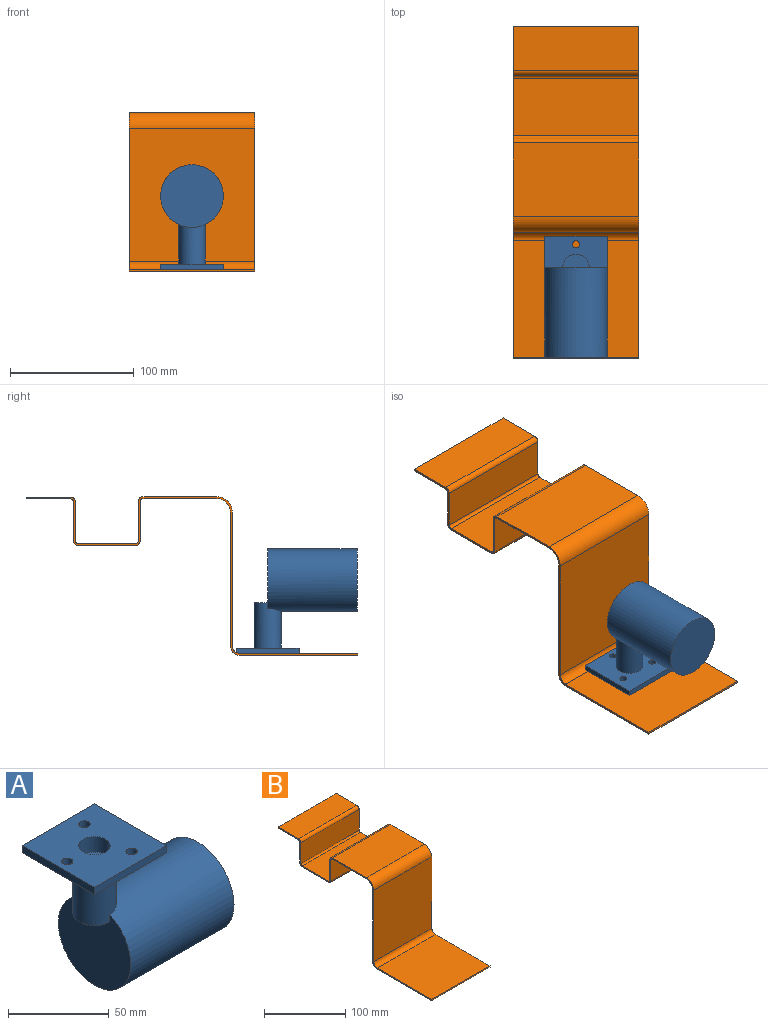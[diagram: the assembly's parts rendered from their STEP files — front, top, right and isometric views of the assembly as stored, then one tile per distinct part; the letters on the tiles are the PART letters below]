
ASSEMBLY  parts=2 mates=1
PART A: 16 faces, bbox 97.8x50.8x84.8 mm
  f0: cylinder r=10.82mm len=36.53mm, axis (0,0,1), area 2291.1mm2, adj f1,f6,f8,f10
  f1: plane 21.65x10.82mm, normal (0,0,-1), area 184mm2, adj f0,f10
  f2: plane 50.8x4.37mm, normal (0,1,0), area 221.9mm2, adj f3,f5,f6,f7
  f3: plane 50.8x4.37mm, normal (-1,0,0), area 221.9mm2, adj f2,f4,f6,f7
  f4: plane 50.8x4.37mm, normal (0,-1,0), area 221.9mm2, adj f3,f5,f6,f7
  f5: plane 50.8x4.37mm, normal (1,0,0), area 221.9mm2, adj f2,f4,f6,f7
  f6: plane 50.8x50.8mm, normal (0,0,-1), area 2138.6mm2, adj f0,f2,f3,f4,f5,f13,f14,f15
  f7: plane 50.8x50.8mm, normal (0,0,1), area 2316mm2, adj f2,f3,f4,f5,f11,f13,f14,f15
  f8: cylinder r=25.37mm len=72.39mm, axis (-1,0,0), area 11349.6mm2, adj f0,f9,f10
  f9: plane 50.74x50.74mm, normal (1,0,0), area 2021.6mm2, adj f8
  f10: plane 50.74x48.31mm, normal (-1,0,0), area 1890.1mm2, adj f0,f1,f8
  f11: cylinder r=7.79mm len=15.58mm, axis (0,0,1), area 459.9mm2, adj f7,f12
  f12: plane 15.58x15.58mm, normal (0,0,1), area 190.6mm2, adj f11
  f13: cylinder r=2.8mm len=5.61mm, axis (0,0,1), area 76.9mm2, adj f6,f7
  f14: cylinder r=2.8mm len=5.61mm, axis (0,0,1), area 76.9mm2, adj f6,f7
  f15: cylinder r=2.8mm len=5.61mm, axis (0,0,1), area 76.9mm2, adj f6,f7
PART B: 54 faces, bbox 101.6x268.5x128.6 mm
  f0: plane 95.25x1.59mm, normal (-1,0,0), area 151.2mm2, adj f2,f3,f4,f50
  f1: plane 95.25x1.59mm, normal (1,0,0), area 151.2mm2, adj f2,f3,f4,f51
  f2: plane 101.6x1.59mm, normal (0,-1,0), area 161.3mm2, adj f0,f1,f3,f4
  f3: plane 101.6x95.25mm, normal (0,0,-1), area 9677.4mm2, adj f0,f1,f2,f52
  f4: plane 101.6x95.25mm, normal (0,0,1), area 9677.4mm2, adj f0,f1,f2,f53
  f5: plane 107.95x1.59mm, normal (-1,0,0), area 171.4mm2, adj f7,f8,f46,f50
  f6: plane 107.95x1.59mm, normal (1,0,0), area 171.4mm2, adj f7,f8,f47,f51
  f7: plane 107.95x101.6mm, normal (0,1,0), area 10967.7mm2, adj f5,f6,f48,f52
  f8: plane 107.95x101.6mm, normal (0,-1,0), area 10967.7mm2, adj f5,f6,f49,f53
  f9: plane 59.63x1.59mm, normal (-1,0,0), area 94.7mm2, adj f11,f12,f43,f46
  f10: plane 59.63x1.59mm, normal (1,0,0), area 94.7mm2, adj f11,f12,f42,f47
  f11: plane 101.6x59.63mm, normal (0,0,-1), area 6058.1mm2, adj f9,f10,f45,f48
  f12: plane 101.6x59.63mm, normal (0,0,1), area 6058.1mm2, adj f9,f10,f44,f49
  f13: plane 31.94x1.59mm, normal (-1,0,0), area 50.7mm2, adj f15,f16,f39,f43
  f14: plane 31.94x1.59mm, normal (1,0,0), area 50.7mm2, adj f15,f16,f38,f42
  f15: plane 101.6x31.94mm, normal (0,-1,0), area 3245.2mm2, adj f13,f14,f40,f45
  f16: plane 101.6x31.94mm, normal (0,1,0), area 3245.2mm2, adj f13,f14,f41,f44
  f17: plane 46.23x1.59mm, normal (-1,0,0), area 73.4mm2, adj f19,f20,f35,f39
  f18: plane 46.23x1.59mm, normal (1,0,0), area 73.4mm2, adj f19,f20,f34,f38
  f19: plane 101.6x46.23mm, normal (0,0,-1), area 4696.8mm2, adj f17,f18,f36,f40
  f20: plane 101.6x46.23mm, normal (0,0,1), area 4696.8mm2, adj f17,f18,f37,f41
  f21: plane 31.58x1.59mm, normal (-1,0,0), area 50.1mm2, adj f23,f24,f31,f35
  f22: plane 31.58x1.59mm, normal (1,0,0), area 50.1mm2, adj f23,f24,f30,f34
  f23: plane 101.6x31.58mm, normal (0,1,0), area 3208.3mm2, adj f21,f22,f33,f36
  f24: plane 101.6x31.58mm, normal (0,-1,0), area 3208.3mm2, adj f21,f22,f32,f37
  f25: plane 36.04x1.59mm, normal (-1,0,0), area 57.2mm2, adj f26,f28,f29,f31
  f26: plane 101.6x1.59mm, normal (0,1,0), area 161.3mm2, adj f25,f27,f28,f29
  f27: plane 36.04x1.59mm, normal (1,0,0), area 57.2mm2, adj f26,f28,f29,f30
  f28: plane 101.6x36.04mm, normal (0,0,-1), area 3661.7mm2, adj f25,f26,f27,f33
  f29: plane 101.6x36.04mm, normal (0,0,1), area 3661.7mm2, adj f25,f26,f27,f32
  f30: plane 3.87x3.87mm, normal (1,0,0), area 7.7mm2, adj f22,f27,f32,f33
  f31: plane 3.87x3.87mm, normal (-1,0,0), area 7.7mm2, adj f21,f25,f32,f33
  f32: cylinder r=3.87mm len=101.6mm, axis (1,0,0), area 618.2mm2, adj f24,f29,f30,f31
  f33: cylinder r=2.29mm len=101.6mm, axis (1,0,0), area 364.8mm2, adj f23,f28,f30,f31
  f34: plane 3.87x3.87mm, normal (1,0,0), area 7.7mm2, adj f18,f22,f36,f37
  f35: plane 3.87x3.87mm, normal (-1,0,0), area 7.7mm2, adj f17,f21,f36,f37
  f36: cylinder r=3.87mm len=101.6mm, axis (1,0,0), area 618.2mm2, adj f19,f23,f34,f35
  f37: cylinder r=2.29mm len=101.6mm, axis (1,0,0), area 364.8mm2, adj f20,f24,f34,f35
  f38: plane 3.87x3.87mm, normal (1,0,0), area 7.7mm2, adj f14,f18,f40,f41
  f39: plane 3.87x3.87mm, normal (-1,0,0), area 7.7mm2, adj f13,f17,f40,f41
  f40: cylinder r=3.87mm len=101.6mm, axis (1,0,0), area 618.2mm2, adj f15,f19,f38,f39
  f41: cylinder r=2.29mm len=101.6mm, axis (1,0,0), area 364.8mm2, adj f16,f20,f38,f39
  f42: plane 3.87x3.87mm, normal (1,0,0), area 7.7mm2, adj f10,f14,f44,f45
  f43: plane 3.87x3.87mm, normal (-1,0,0), area 7.7mm2, adj f9,f13,f44,f45
  f44: cylinder r=3.87mm len=101.6mm, axis (1,0,0), area 618.2mm2, adj f12,f16,f42,f43
  f45: cylinder r=2.29mm len=101.6mm, axis (1,0,0), area 364.8mm2, adj f11,f15,f42,f43
  f46: plane 12.7x12.7mm, normal (-1,0,0), area 29.7mm2, adj f5,f9,f48,f49
  f47: plane 12.7x12.7mm, normal (1,0,0), area 29.7mm2, adj f6,f10,f48,f49
  f48: cylinder r=11.11mm len=101.6mm, axis (1,0,0), area 1773.5mm2, adj f7,f11,f46,f47
  f49: cylinder r=12.7mm len=101.6mm, axis (1,0,0), area 2026.8mm2, adj f8,f12,f46,f47
  f50: plane 7.94x7.94mm, normal (-1,0,0), area 17.8mm2, adj f0,f5,f52,f53
  f51: plane 7.94x7.94mm, normal (1,0,0), area 17.8mm2, adj f1,f6,f52,f53
  f52: cylinder r=7.94mm len=101.6mm, axis (1,0,0), area 1266.8mm2, adj f3,f7,f50,f51
  f53: cylinder r=6.35mm len=101.6mm, axis (1,0,0), area 1013.4mm2, adj f4,f8,f50,f51
PLACE A rot(axis=(0.71,-0.71,0),180deg) t=(1,-60.94,-63.13)mm
PLACE B t=(1,69.78,-63.13)mm fixed
MATE parallel B.f4 <-> A.f7  axis (0,0,1) through (1,-86.34,-63.13)mm
